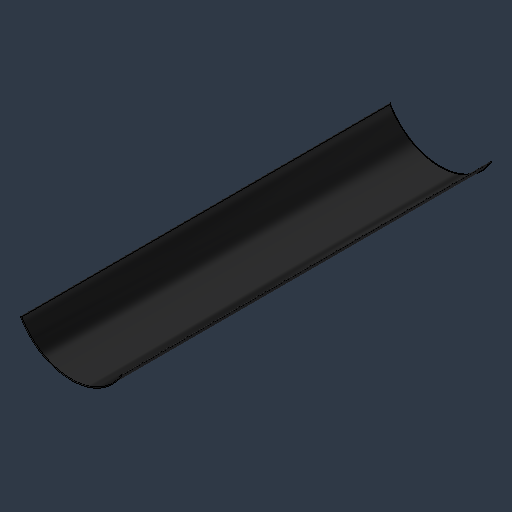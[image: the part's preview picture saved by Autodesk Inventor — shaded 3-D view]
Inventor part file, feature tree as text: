
AUTODESK INVENTOR PART (.ipt)
format: ipt  version: 2024.3 (Build 283343000, 343)  size: 206,848 bytes
history: native  units: mm (DEFAULTED — no unit token found)
features: sweep x1
ambient origin geometry x8: Origin, YZ Plane, XZ Plane, XY Plane, X Axis, Y Axis, Z Axis, Center Point
bodies: Solid1 (feature_tree)
feature tree (1):
  sweep  "Sweep1"
